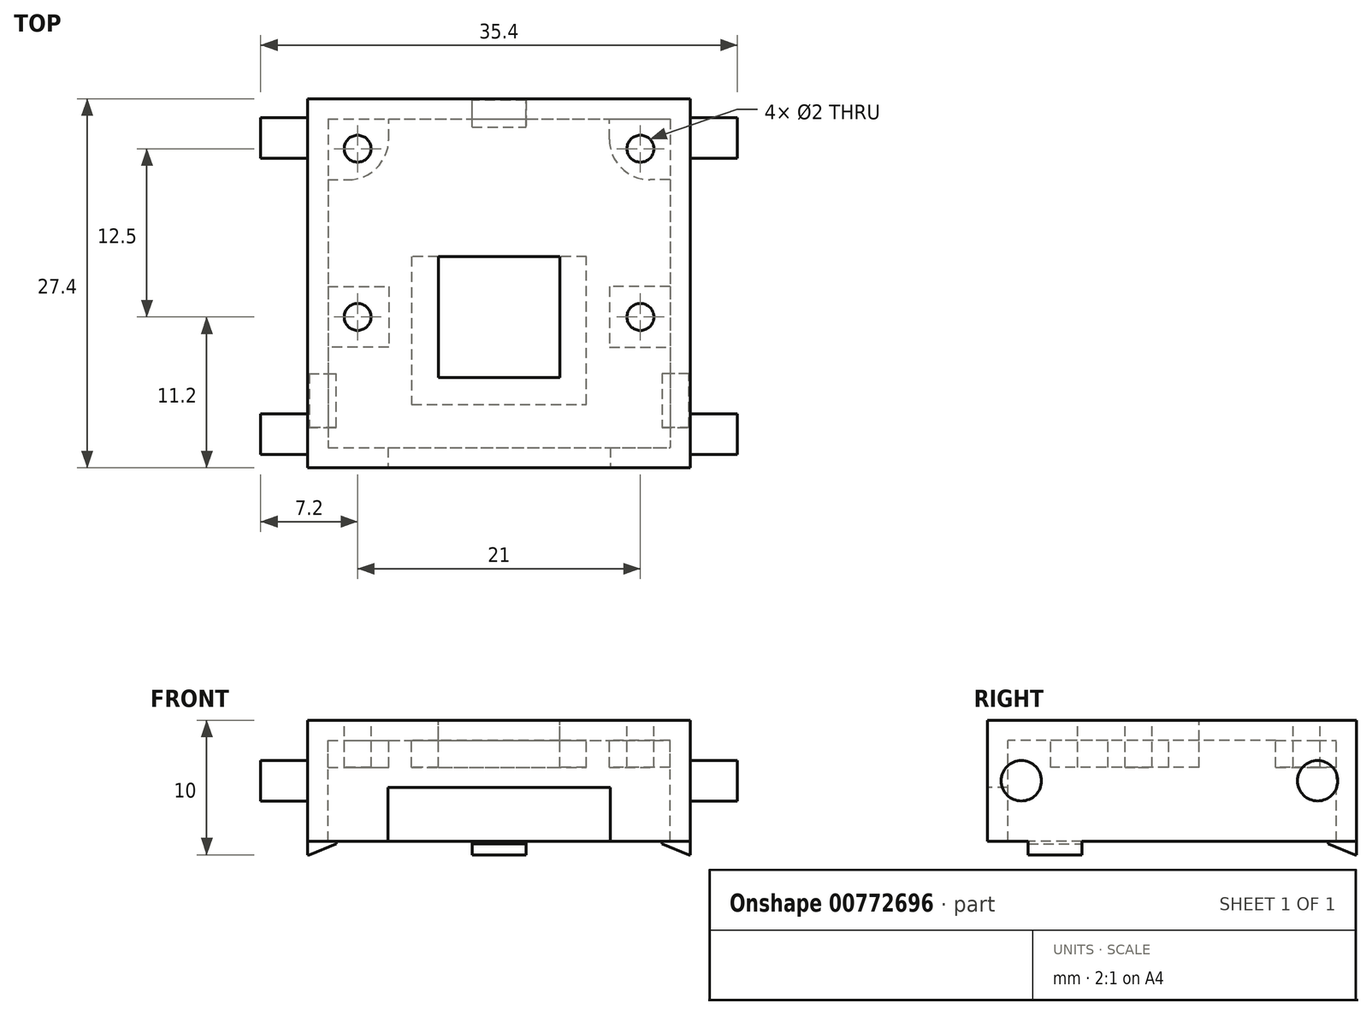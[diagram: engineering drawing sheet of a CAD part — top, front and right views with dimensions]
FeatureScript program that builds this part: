
annotation { "Feature Type Name" : "Feature", "Feature Type Description" : "" }
export const myFeature = defineFeature(function(context is Context, id is Id, definition is map)
    precondition{}
    {
        {
            var Q0;
            Q0=qCreatedBy(makeId("Top.planeOp"),FACE);
            var sketch = newSketch(context, id + "F0", { "sketchPlane" : qUnion([Q0])});
            skLineSegment(sketch, "E0.bottom", {"start": v(-12.5, 12) * mm, "end": v(12.5, 12) * mm, "construction": true});
            skLineSegment(sketch, "E0.top", {"start": v(-12.5, -12) * mm, "end": v(12.5, -12) * mm, "construction": true});
            skLineSegment(sketch, "E0.left", {"start": v(-12.5, 12) * mm, "end": v(-12.5, -12) * mm, "construction": true});
            skLineSegment(sketch, "E0.right", {"start": v(12.5, 12) * mm, "end": v(12.5, -12) * mm, "construction": true});
            skLineSegment(sketch, "E1.bottom", {"start": v(-4.5, 2) * mm, "end": v(4.5, 2) * mm});
            skLineSegment(sketch, "E1.top", {"start": v(-4.5, -7) * mm, "end": v(4.5, -7) * mm});
            skLineSegment(sketch, "E1.left", {"start": v(-4.5, 2) * mm, "end": v(-4.5, -7) * mm});
            skLineSegment(sketch, "E1.right", {"start": v(4.5, 2) * mm, "end": v(4.5, -7) * mm});
            skLineSegment(sketch, "E2", {"start": v(-16.59, -2.5) * mm, "end": v(16.18, -2.5) * mm, "construction": true});
            skCircle(sketch, "E3", {"center": v(10.5, -2.5) * mm, "radius": 1 * mm});
            skCircle(sketch, "E4", {"center": v(-10.5, -2.5) * mm, "radius": 1 * mm});
            skCircle(sketch, "E5", {"center": v(-10.5, 10) * mm, "radius": 1 * mm});
            skCircle(sketch, "E6", {"center": v(10.5, 10) * mm, "radius": 1 * mm});
            skLineSegment(sketch, "E7", {"start": v(-4.5, 2) * mm, "end": v(-6.5, 2) * mm});
            skLineSegment(sketch, "E8", {"start": v(-6.5, 2) * mm, "end": v(-6.5, -9) * mm});
            skLineSegment(sketch, "E9", {"start": v(-6.5, -9) * mm, "end": v(6.5, -9) * mm});
            skLineSegment(sketch, "E10", {"start": v(6.5, -9) * mm, "end": v(6.5, 2) * mm});
            skLineSegment(sketch, "E11", {"start": v(6.5, 2) * mm, "end": v(4.5, 2) * mm});
            skLineSegment(sketch, "E12.bottom", {"start": v(-12.7, 12.2) * mm, "end": v(12.7, 12.2) * mm});
            skLineSegment(sketch, "E12.left", {"start": v(-12.7, 12.2) * mm, "end": v(-12.7, -12.2) * mm});
            skLineSegment(sketch, "E12.right", {"start": v(12.7, 12.2) * mm, "end": v(12.7, -12.2) * mm});
            skLineSegment(sketch, "E13.bottom", {"start": v(-14.2, 13.7) * mm, "end": v(14.2, 13.7) * mm});
            skLineSegment(sketch, "E13.left", {"start": v(-14.2, 13.7) * mm, "end": v(-14.2, -13.7) * mm});
            skLineSegment(sketch, "E13.right", {"start": v(14.2, 13.7) * mm, "end": v(14.2, -13.7) * mm});
            skLineSegment(sketch, "E14", {"start": v(-12.7, -12.2) * mm, "end": v(-8.25, -12.2) * mm});
            skLineSegment(sketch, "E15", {"start": v(-12.7, 7.7) * mm, "end": v(-8.2, 7.7) * mm});
            skLineSegment(sketch, "E16", {"start": v(-8.2, 7.7) * mm, "end": v(-8.2, 12.2) * mm});
            skLineSegment(sketch, "E17", {"start": v(-12.7, -0.25) * mm, "end": v(-8.2, -0.25) * mm});
            skLineSegment(sketch, "E18", {"start": v(-8.2, -0.25) * mm, "end": v(-8.2, -4.75) * mm});
            skLineSegment(sketch, "E19", {"start": v(-8.2, -4.75) * mm, "end": v(-12.7, -4.75) * mm});
            skLineSegment(sketch, "E20.MirrorCS", {"start": v(8.2, 7.7) * mm, "end": v(8.2, 12.2) * mm});
            skLineSegment(sketch, "E21.MirrorCS", {"start": v(12.7, 7.7) * mm, "end": v(8.2, 7.7) * mm});
            skLineSegment(sketch, "E22.MirrorCS", {"start": v(8.2, -4.75) * mm, "end": v(12.7, -4.75) * mm});
            skLineSegment(sketch, "E23.MirrorCS", {"start": v(12.7, -0.25) * mm, "end": v(8.2, -0.25) * mm});
            skLineSegment(sketch, "E24.MirrorCS", {"start": v(8.2, -0.25) * mm, "end": v(8.2, -4.75) * mm});
            skLineSegment(sketch, "E25", {"start": v(8.25, -12.2) * mm, "end": v(8.25, -13.7) * mm});
            skLineSegment(sketch, "E26", {"start": v(-8.25, -12.2) * mm, "end": v(-8.25, -13.7) * mm});
            skLineSegment(sketch, "E27.trimOffspring", {"start": v(8.25, -12.2) * mm, "end": v(12.7, -12.2) * mm});
            skLineSegment(sketch, "E28", {"start": v(8.25, -13.7) * mm, "end": v(14.2, -13.7) * mm});
            skLineSegment(sketch, "E29", {"start": v(-8.25, -13.7) * mm, "end": v(-14.2, -13.7) * mm});
            skLineSegment(sketch, "E30", {"start": v(-8.25, -13.7) * mm, "end": v(8.25, -13.7) * mm});
            skLineSegment(sketch, "E31", {"start": v(-8.25, -12.2) * mm, "end": v(8.25, -12.2) * mm});
            skSolve(sketch);
        }
        {
            var Q0;
            Q0=makeQuery(id+"F0.imprint","IMPRINT",FACE,{"disambiguationData":[TD([[makeQuery(id+"F0.imprint","IMPRINT",EDGE,{"derivedFrom":sQuery(id+"F0.wireOp",EDGE,"R9PUv51m-K8Uj-Q1tC-1k26-saT1gila1T0l")}),-1.0]])]});
            var Q1;
            Q1=makeQuery(id+"F0.imprint","IMPRINT",FACE,{"disambiguationData":[TD([[makeQuery(id+"F0.imprint","IMPRINT",EDGE,{"derivedFrom":sQuery(id+"F0.wireOp",EDGE,"E1.bottom")}),1.0]])]});
            extrude(context, id + "F1", {"entities" : qUnion([Q0, Q1]), "oppositeDirection" : true, "depth" : 1.5 * mm, "offsetDistance" : 25 * mm});
        }
        {
            var Q0;
            Q0=makeQuery(id+"F0.imprint","IMPRINT",FACE,{"disambiguationData":[TD([[makeQuery(id+"F0.imprint","IMPRINT",EDGE,{"derivedFrom":sQuery(id+"F0.wireOp",EDGE,"E13.bottom")}),-1.0]])]});
            extrude(context, id + "F2", {"entities" : qUnion([Q0]), "oppositeDirection" : true, "depth" : 9 * mm, "offsetDistance" : 25 * mm});
        }
        {
            var Q0;
            Q0=makeQuery(id+"F0.imprint","IMPRINT",FACE,{"disambiguationData":[TD([[makeQuery(id+"F0.imprint","IMPRINT",EDGE,{"derivedFrom":sQuery(id+"F0.wireOp",EDGE,"E6")}),-1.0]])]});
            var Q1;
            Q1=makeQuery(id+"F0.imprint","IMPRINT",FACE,{"disambiguationData":[TD([[makeQuery(id+"F0.imprint","IMPRINT",EDGE,{"derivedFrom":sQuery(id+"F0.wireOp",EDGE,"E3")}),-1.0]])]});
            var Q2;
            Q2=makeQuery(id+"F0.imprint","IMPRINT",FACE,{"disambiguationData":[TD([[makeQuery(id+"F0.imprint","IMPRINT",EDGE,{"derivedFrom":sQuery(id+"F0.wireOp",EDGE,"E1.top")}),-1.0]])]});
            var Q3;
            Q3=makeQuery(id+"F0.imprint","IMPRINT",FACE,{"disambiguationData":[TD([[makeQuery(id+"F0.imprint","IMPRINT",EDGE,{"derivedFrom":sQuery(id+"F0.wireOp",EDGE,"E5")}),-1.0]])]});
            var Q4;
            Q4=makeQuery(id+"F0.imprint","IMPRINT",FACE,{"disambiguationData":[TD([[makeQuery(id+"F0.imprint","IMPRINT",EDGE,{"derivedFrom":sQuery(id+"F0.wireOp",EDGE,"E4")}),-1.0]])]});
            extrude(context, id + "F3", {"entities" : qUnion([Q0, Q1, Q2, Q3, Q4]), "oppositeDirection" : true, "depth" : 3.5 * mm, "offsetDistance" : 25 * mm});
        }
        {
            var Q0;
            Q0=makeQuery(id+"F0.imprint","IMPRINT",FACE,{"disambiguationData":[TD([[makeQuery(id+"F0.imprint","IMPRINT",EDGE,{"derivedFrom":sQuery(id+"F0.wireOp",EDGE,"E25")}),-1.0]])]});
            extrude(context, id + "F4", {"entities" : qUnion([Q0]), "operationType" : NewBodyOperationType.ADD, "oppositeDirection" : true, "depth" : 5 * mm, "offsetDistance" : 25 * mm});
        }
        {
            var Q0;
            Q0=makeQuery(id+"F2.opExtrude","SWEPT_FACE",FACE,{"disambiguationData":[OSD([sQuery(id+"F0.wireOp",EDGE,"E13.left")])]});
            var sketch = newSketch(context, id + "F5", { "sketchPlane" : qUnion([Q0])});
            skLineSegment(sketch, "E32", {"start": v(-14.64, -4.5) * mm, "end": v(15.28, -4.5) * mm, "construction": true});
            skCircle(sketch, "E33", {"center": v(-10.8, -4.5) * mm, "radius": 1.5 * mm});
            skCircle(sketch, "E34", {"center": v(11.2, -4.5) * mm, "radius": 1.5 * mm});
            skSolve(sketch);
        }
        {
            var Q0;
            Q0=makeQuery(id+"F5.imprint","IMPRINT",FACE,{"disambiguationData":[TD([[makeQuery(id+"F5.imprint","IMPRINT",EDGE,{"derivedFrom":sQuery(id+"F5.wireOp",EDGE,"E34")}),1.0]])]});
            var Q1;
            Q1=makeQuery(id+"F5.imprint","IMPRINT",FACE,{"disambiguationData":[TD([[makeQuery(id+"F5.imprint","IMPRINT",EDGE,{"derivedFrom":sQuery(id+"F5.wireOp",EDGE,"E33")}),1.0]])]});
            extrude(context, id + "F6", {"entities" : qUnion([Q0, Q1]), "operationType" : NewBodyOperationType.ADD, "depth" : 3.5 * mm, "offsetDistance" : 25 * mm});
        }
        {
            var Q0;
            Q0=makeQuery(id+"F1.opExtrude","SWEPT_BODY",BODY,{"disambiguationData":[OSD([sQuery(id+"F0.wireOp",EDGE,"E1.bottom"),sQuery(id+"F0.wireOp",EDGE,"E7"),sQuery(id+"F0.wireOp",EDGE,"E8"),sQuery(id+"F0.wireOp",EDGE,"E9"),sQuery(id+"F0.wireOp",EDGE,"E10"),sQuery(id+"F0.wireOp",EDGE,"E11"),sQuery(id+"F0.wireOp",EDGE,"E12.bottom"),sQuery(id+"F0.wireOp",EDGE,"E12.left"),sQuery(id+"F0.wireOp",EDGE,"E12.right"),sQuery(id+"F0.wireOp",EDGE,"E14"),sQuery(id+"F0.wireOp",EDGE,"E15"),sQuery(id+"F0.wireOp",EDGE,"E16"),sQuery(id+"F0.wireOp",EDGE,"E17"),sQuery(id+"F0.wireOp",EDGE,"E18"),sQuery(id+"F0.wireOp",EDGE,"E19"),sQuery(id+"F0.wireOp",EDGE,"E20.MirrorCS"),sQuery(id+"F0.wireOp",EDGE,"E21.MirrorCS"),sQuery(id+"F0.wireOp",EDGE,"E22.MirrorCS"),sQuery(id+"F0.wireOp",EDGE,"E23.MirrorCS"),sQuery(id+"F0.wireOp",EDGE,"E24.MirrorCS"),sQuery(id+"F0.wireOp",EDGE,"E27.trimOffspring"),sQuery(id+"F0.wireOp",EDGE,"E31")])]});
            var Q1;
            Q1=qCreatedBy(makeId("Right.planeOp"),FACE);
            mirror(context, id + "F7", {"operationType" : NewBodyOperationType.ADD, "entities" : qUnion([Q0]), "mirrorPlane" : qUnion([Q1])});
        }
        {
            var Q0;
            Q0=makeQuery(id+"F3.opExtrude","SWEPT_EDGE",EDGE,{"disambiguationData":[OSD([sQuery(id+"F0.wireOp",EDGE,"E20.MirrorCS"),sQuery(id+"F0.wireOp",EDGE,"E21.MirrorCS")])]});
            var Q1;
            Q1=makeQuery(id+"F3.opExtrude","SWEPT_EDGE",EDGE,{"disambiguationData":[OSD([sQuery(id+"F0.wireOp",EDGE,"E15"),sQuery(id+"F0.wireOp",EDGE,"E16")])]});
            fillet(context, id + "F8", {"entities" : qUnion([Q0, Q1]), "tangentPropagation" : true, "radius" : 3 * mm, "defaultsChanged" : true, "vertexSettings" : [], "allowEdgeOverflow" : false});
        }
        {
            var Q0;
            Q0=makeQuery(id+"F2.opExtrude","CAP_FACE",FACE,{"disambiguationData":[OSD([sQuery(id+"F0.wireOp",EDGE,"E12.bottom"),sQuery(id+"F0.wireOp",EDGE,"E12.left"),sQuery(id+"F0.wireOp",EDGE,"E12.right"),sQuery(id+"F0.wireOp",EDGE,"E13.bottom"),sQuery(id+"F0.wireOp",EDGE,"E13.left"),sQuery(id+"F0.wireOp",EDGE,"E13.right"),sQuery(id+"F0.wireOp",EDGE,"E14"),sQuery(id+"F0.wireOp",EDGE,"E25"),sQuery(id+"F0.wireOp",EDGE,"E26"),sQuery(id+"F0.wireOp",EDGE,"E27.trimOffspring"),sQuery(id+"F0.wireOp",EDGE,"E28"),sQuery(id+"F0.wireOp",EDGE,"E29")])],"isStart":false});
            var sketch = newSketch(context, id + "F9", { "sketchPlane" : qUnion([Q0])});
            skLineSegment(sketch, "E35.bottom", {"start": v(-14.2, 10.7) * mm, "end": v(-12.1, 10.7) * mm});
            skLineSegment(sketch, "E35.top", {"start": v(-14.2, 6.7) * mm, "end": v(-12.1, 6.7) * mm});
            skLineSegment(sketch, "E35.left", {"start": v(-14.2, 10.7) * mm, "end": v(-14.2, 6.7) * mm});
            skLineSegment(sketch, "E35.right", {"start": v(-12.1, 10.7) * mm, "end": v(-12.1, 6.7) * mm});
            skLineSegment(sketch, "E36.bottom", {"start": v(14.2, 10.7) * mm, "end": v(12.1, 10.7) * mm});
            skLineSegment(sketch, "E36.top", {"start": v(14.2, 6.7) * mm, "end": v(12.1, 6.7) * mm});
            skLineSegment(sketch, "E36.left", {"start": v(14.2, 10.7) * mm, "end": v(14.2, 6.7) * mm});
            skLineSegment(sketch, "E36.right", {"start": v(12.1, 10.7) * mm, "end": v(12.1, 6.7) * mm});
            skLineSegment(sketch, "E37.bottom", {"start": v(-2, -11.6) * mm, "end": v(2, -11.6) * mm});
            skLineSegment(sketch, "E37.top", {"start": v(-2, -13.7) * mm, "end": v(2, -13.7) * mm});
            skLineSegment(sketch, "E37.left", {"start": v(-2, -11.6) * mm, "end": v(-2, -13.7) * mm});
            skLineSegment(sketch, "E37.right", {"start": v(2, -11.6) * mm, "end": v(2, -13.7) * mm});
            skSolve(sketch);
        }
        {
            var Q0;
            {var subQ0=sQuery(id+"F9.wireOp",EDGE,"E35.right");Q0=makeQuery(id+"F9.imprint","IMPRINT",FACE,{"disambiguationData":[TD([[makeQuery(id+"F9.imprint","IMPRINT",EDGE,{"derivedFrom":subQ0}),-1.0]])]});}
            var Q1;
            {var subQ0=sQuery(id+"F9.wireOp",EDGE,"E35.left");Q1=makeQuery(id+"F9.imprint","IMPRINT",FACE,{"disambiguationData":[TD([[makeQuery(id+"F9.imprint","IMPRINT",EDGE,{"derivedFrom":subQ0}),-1.0]])]});}
            var Q2;
            {var subQ0=sQuery(id+"F9.wireOp",EDGE,"E36.right");Q2=makeQuery(id+"F9.imprint","IMPRINT",FACE,{"disambiguationData":[TD([[makeQuery(id+"F9.imprint","IMPRINT",EDGE,{"derivedFrom":subQ0}),1.0]])]});}
            var Q3;
            {var subQ0=sQuery(id+"F9.wireOp",EDGE,"E36.left");Q3=makeQuery(id+"F9.imprint","IMPRINT",FACE,{"disambiguationData":[TD([[makeQuery(id+"F9.imprint","IMPRINT",EDGE,{"derivedFrom":subQ0}),1.0]])]});}
            var Q4;
            {var subQ0=sQuery(id+"F9.wireOp",EDGE,"E37.bottom");Q4=makeQuery(id+"F9.imprint","IMPRINT",FACE,{"disambiguationData":[TD([[makeQuery(id+"F9.imprint","IMPRINT",EDGE,{"derivedFrom":subQ0}),-1.0]])]});}
            var Q5;
            {var subQ0=sQuery(id+"F9.wireOp",EDGE,"E37.top");Q5=makeQuery(id+"F9.imprint","IMPRINT",FACE,{"disambiguationData":[TD([[makeQuery(id+"F9.imprint","IMPRINT",EDGE,{"derivedFrom":subQ0}),1.0]])]});}
            extrude(context, id + "F10", {"entities" : qUnion([Q0, Q1, Q2, Q3, Q4, Q5]), "operationType" : NewBodyOperationType.ADD, "depth" : 1 * mm, "offsetDistance" : 25 * mm});
        }
        {
            var Q0;
            Q0=makeQuery(id+"F10.opExtrude","CAP_EDGE",EDGE,{"disambiguationData":[OSD([sQuery(id+"F9.wireOp",EDGE,"E35.right")])],"isStart":false});
            var Q1;
            Q1=makeQuery(id+"F10.opExtrude","CAP_EDGE",EDGE,{"disambiguationData":[OSD([sQuery(id+"F9.wireOp",EDGE,"E37.bottom")])],"isStart":false});
            chamfer(context, id + "F11", {"entities" : qUnion([Q0, Q1]), "chamferType" : ChamferType.TWO_OFFSETS, "width1" : 0.8 * mm, "oppositeDirection" : false, "width2" : 2 * mm, "tangentPropagation" : true});
        }
        {
            var Q0;
            Q0=makeQuery(id+"F10.opExtrude","CAP_EDGE",EDGE,{"disambiguationData":[OSD([sQuery(id+"F9.wireOp",EDGE,"E36.right")])],"isStart":false});
            chamfer(context, id + "F12", {"entities" : qUnion([Q0]), "chamferType" : ChamferType.TWO_OFFSETS, "width1" : 2 * mm, "oppositeDirection" : false, "width2" : 0.8 * mm, "tangentPropagation" : true});
        }
    });
